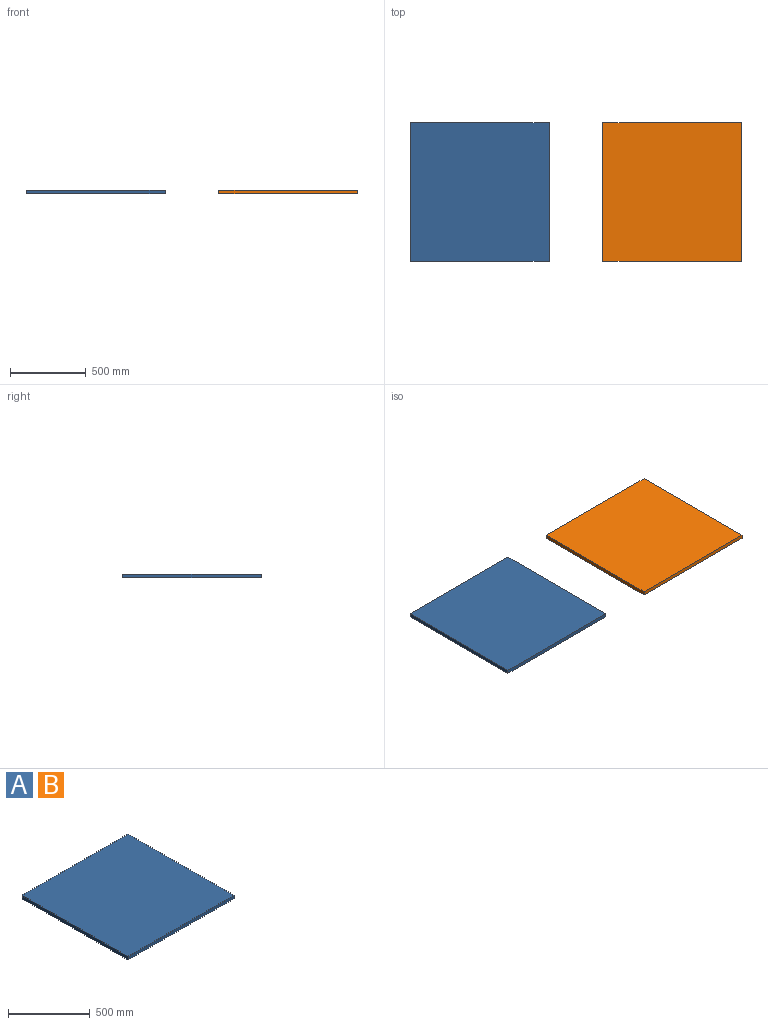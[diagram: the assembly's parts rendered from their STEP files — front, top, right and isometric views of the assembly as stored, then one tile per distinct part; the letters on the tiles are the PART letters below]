
ASSEMBLY  parts=2 mates=1
PART A: 6 faces, bbox 914.4x914.4x25.4 mm
  f0: plane 914.4x25.4mm, normal (0,1,0), area 23225.8mm2, adj f1,f3,f4,f5
  f1: plane 914.4x25.4mm, normal (-1,0,0), area 23225.8mm2, adj f0,f2,f4,f5
  f2: plane 914.4x25.4mm, normal (0,-1,0), area 23225.8mm2, adj f1,f3,f4,f5
  f3: plane 914.4x25.4mm, normal (1,0,0), area 23225.8mm2, adj f0,f2,f4,f5
  f4: plane 914.4x914.4mm, normal (0,0,1), area 836127.4mm2, adj f0,f1,f2,f3
  f5: plane 914.4x914.4mm, normal (0,0,-1), area 836127.4mm2, adj f0,f1,f2,f3
PART B: same geometry as A
PLACE A t=(-783.94,-294.26,134.6)mm
PLACE B t=(486.06,-294.26,134.6)mm
MATE planar A.f2 <-> B.f2  axis (0,-1,0) through (638.46,-294.26,147.3)mm
